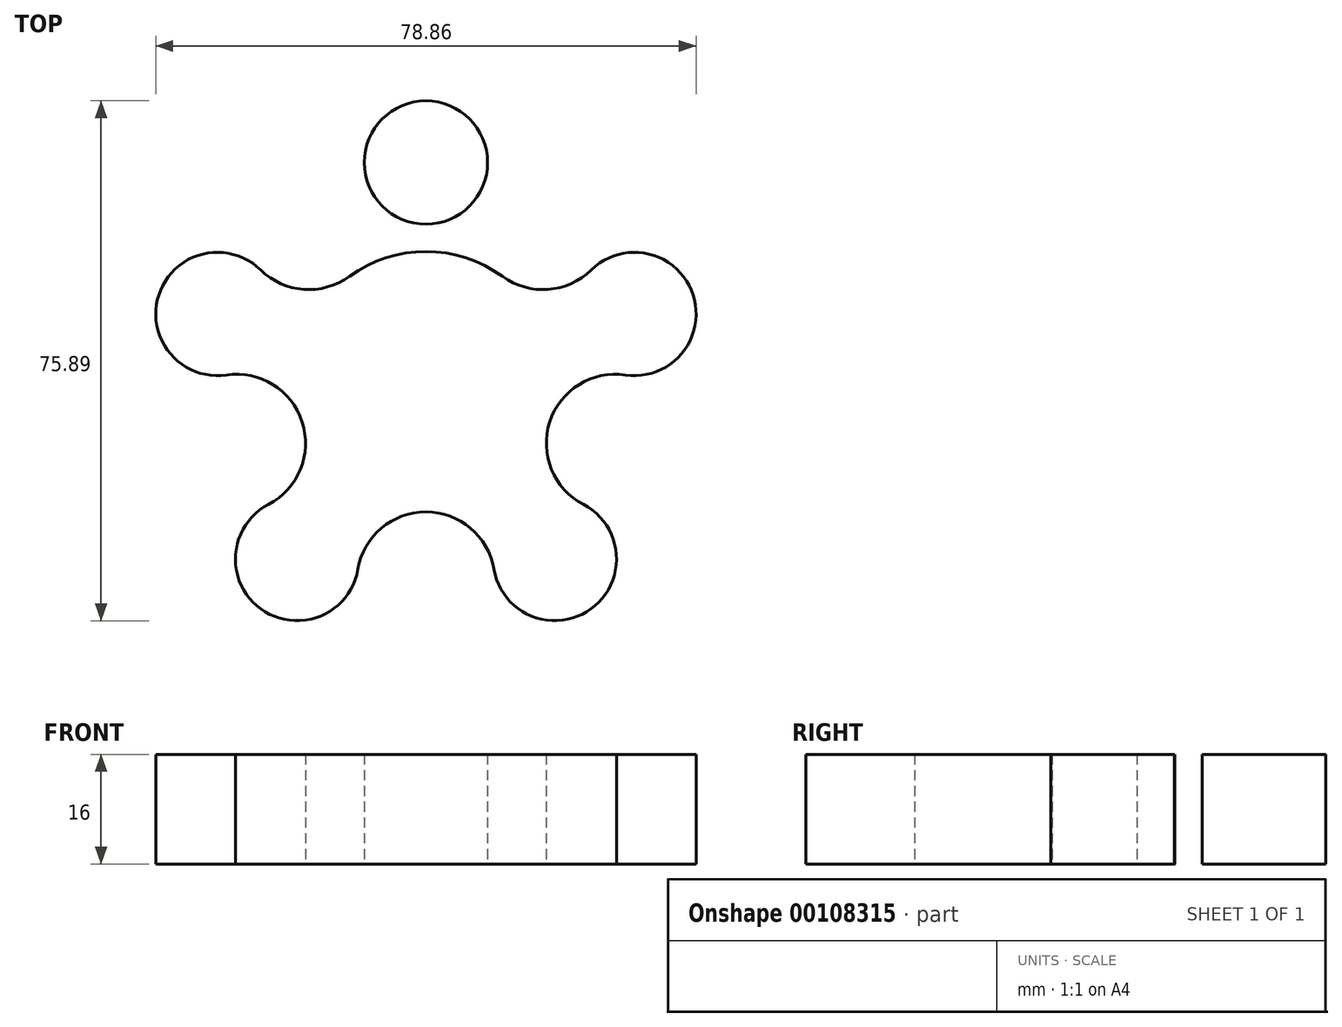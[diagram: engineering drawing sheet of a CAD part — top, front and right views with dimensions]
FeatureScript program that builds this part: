
annotation { "Feature Type Name" : "Feature", "Feature Type Description" : "" }
export const myFeature = defineFeature(function(context is Context, id is Id, definition is map)
    precondition{}
    {
        {
            var Q0;
            Q0=qCreatedBy(makeId("Top.planeOp"),FACE);
            var sketch = newSketch(context, id + "F0", { "sketchPlane" : qUnion([Q0])});
            skCircle(sketch, "E0", {"center": v(0, 0) * mm, "radius": 19 * mm});
            skLineSegment(sketch, "E1", {"start": v(0, 0) * mm, "end": v(22.05, 30.35) * mm, "construction": true});
            skLineSegment(sketch, "E2", {"start": v(-22.13, 41) * mm, "end": v(0, 41) * mm, "construction": true});
            skLineSegment(sketch, "E3", {"start": v(11.17, 15.37) * mm, "end": v(26.44, 4.28) * mm, "construction": true});
            skCircle(sketch, "E4", {"center": v(0, 32) * mm, "radius": 9 * mm});
            skArc(sketch, "E5", {"start": v(11.17, 15.37) * mm, "mid": v(7.3, 21.12) * mm, "end": v(8.06, 28) * mm});
            skArc(sketch, "E6.MirrorCS", {"start": v(-11.17, 15.37) * mm, "mid": v(-7.3, 21.12) * mm, "end": v(-8.06, 28) * mm});
            skCircle(sketch, "E7.1.0", {"center": v(-30.43, 9.89) * mm, "radius": 9 * mm});
            skArc(sketch, "E7.1.1", {"start": v(-18.07, -5.87) * mm, "mid": v(-22.34, -0.42) * mm, "end": v(-29.12, 0.98) * mm});
            skArc(sketch, "E7.1.3", {"start": v(-11.17, 15.37) * mm, "mid": v(-17.83, 13.47) * mm, "end": v(-24.14, 16.32) * mm});
            skCircle(sketch, "E7.2.0", {"center": v(-18.8, -25.89) * mm, "radius": 9 * mm});
            skArc(sketch, "E7.2.1", {"start": v(0, -19) * mm, "mid": v(-6.5, -21.38) * mm, "end": v(-9.94, -27.4) * mm});
            skArc(sketch, "E7.2.3", {"start": v(-18.07, -5.87) * mm, "mid": v(-18.32, -12.8) * mm, "end": v(-22.98, -17.91) * mm});
            skCircle(sketch, "E7.3.0", {"center": v(18.8, -25.89) * mm, "radius": 9 * mm});
            skArc(sketch, "E7.3.1", {"start": v(18.07, -5.87) * mm, "mid": v(18.32, -12.8) * mm, "end": v(22.98, -17.91) * mm});
            skArc(sketch, "E7.3.3", {"start": v(0, -19) * mm, "mid": v(6.5, -21.38) * mm, "end": v(9.94, -27.4) * mm});
            skCircle(sketch, "E7.4.0", {"center": v(30.43, 9.89) * mm, "radius": 9 * mm});
            skArc(sketch, "E7.4.1", {"start": v(11.17, 15.37) * mm, "mid": v(17.83, 13.47) * mm, "end": v(24.14, 16.32) * mm});
            skArc(sketch, "E7.4.3", {"start": v(18.07, -5.87) * mm, "mid": v(22.34, -0.42) * mm, "end": v(29.12, 0.98) * mm});
            skSolve(sketch);
        }
        {
            var Q0;
            {var subQ0=sQuery(id+"F0.wireOp",EDGE,"E4");var subQ1=makeQuery(id+"F0.imprint","INTERSECT",VERTEX,{"derivedFrom":[subQ0,sQuery(id+"F0.wireOp",EDGE,"E5")]});Q0=makeQuery(id+"F0.imprint","IMPRINT",FACE,{"disambiguationData":[TD([[makeQuery(id+"F0.imprint","IMPRINT",EDGE,{"disambiguationData":[TD([[subQ1,1.0]])],"derivedFrom":subQ0}),1.0]])]});}
            var Q1;
            {var subQ0=sQuery(id+"F0.wireOp",EDGE,"E7.4.0");var subQ1=makeQuery(id+"F0.imprint","INTERSECT",VERTEX,{"derivedFrom":[subQ0,sQuery(id+"F0.wireOp",EDGE,"E7.4.1")]});Q1=makeQuery(id+"F0.imprint","IMPRINT",FACE,{"disambiguationData":[TD([[makeQuery(id+"F0.imprint","IMPRINT",EDGE,{"disambiguationData":[TD([[subQ1,-1.0]])],"derivedFrom":subQ0}),1.0]])]});}
            var Q2;
            {var subQ0=sQuery(id+"F0.wireOp",EDGE,"E7.3.0");var subQ1=makeQuery(id+"F0.imprint","INTERSECT",VERTEX,{"derivedFrom":[subQ0,sQuery(id+"F0.wireOp",EDGE,"E7.3.1")]});Q2=makeQuery(id+"F0.imprint","IMPRINT",FACE,{"disambiguationData":[TD([[makeQuery(id+"F0.imprint","IMPRINT",EDGE,{"disambiguationData":[TD([[subQ1,-1.0]])],"derivedFrom":subQ0}),1.0]])]});}
            var Q3;
            {var subQ0=sQuery(id+"F0.wireOp",EDGE,"E7.2.0");var subQ1=makeQuery(id+"F0.imprint","INTERSECT",VERTEX,{"derivedFrom":[subQ0,sQuery(id+"F0.wireOp",EDGE,"E7.2.1")]});Q3=makeQuery(id+"F0.imprint","IMPRINT",FACE,{"disambiguationData":[TD([[makeQuery(id+"F0.imprint","IMPRINT",EDGE,{"disambiguationData":[TD([[subQ1,-1.0]])],"derivedFrom":subQ0}),1.0]])]});}
            var Q4;
            {var subQ0=sQuery(id+"F0.wireOp",EDGE,"E7.1.0");var subQ1=makeQuery(id+"F0.imprint","INTERSECT",VERTEX,{"derivedFrom":[subQ0,sQuery(id+"F0.wireOp",EDGE,"E7.1.1")]});Q4=makeQuery(id+"F0.imprint","IMPRINT",FACE,{"disambiguationData":[TD([[makeQuery(id+"F0.imprint","IMPRINT",EDGE,{"disambiguationData":[TD([[subQ1,-1.0]])],"derivedFrom":subQ0}),1.0]])]});}
            var Q5;
            {var subQ0=sQuery(id+"F0.wireOp",EDGE,"E0");var subQ5=makeQuery(id+"F0.imprint","INTERSECT",VERTEX,{"derivedFrom":[subQ0,sQuery(id+"F0.wireOp",EDGE,"E5"),sQuery(id+"F0.wireOp",EDGE,"E7.4.1")]});Q5=makeQuery(id+"F0.imprint","IMPRINT",FACE,{"disambiguationData":[TD([[makeQuery(id+"F0.imprint","IMPRINT",EDGE,{"disambiguationData":[TD([[subQ5,-1.0]])],"derivedFrom":subQ0}),1.0]])]});}
            var Q6;
            {var subQ2=sQuery(id+"F0.wireOp",EDGE,"E7.3.1");Q6=makeQuery(id+"F0.imprint","IMPRINT",FACE,{"disambiguationData":[TD([[makeQuery(id+"F0.imprint","IMPRINT",EDGE,{"derivedFrom":subQ2}),-1.0]])]});}
            var Q7;
            {var subQ2=sQuery(id+"F0.wireOp",EDGE,"E7.2.1");Q7=makeQuery(id+"F0.imprint","IMPRINT",FACE,{"disambiguationData":[TD([[makeQuery(id+"F0.imprint","IMPRINT",EDGE,{"derivedFrom":subQ2}),-1.0]])]});}
            var Q8;
            {var subQ2=sQuery(id+"F0.wireOp",EDGE,"E7.1.1");Q8=makeQuery(id+"F0.imprint","IMPRINT",FACE,{"disambiguationData":[TD([[makeQuery(id+"F0.imprint","IMPRINT",EDGE,{"derivedFrom":subQ2}),-1.0]])]});}
            var Q9;
            {var subQ0=sQuery(id+"F0.wireOp",EDGE,"E5");Q9=makeQuery(id+"F0.imprint","IMPRINT",FACE,{"disambiguationData":[TD([[makeQuery(id+"F0.imprint","IMPRINT",EDGE,{"derivedFrom":subQ0}),1.0]])]});}
            var Q10;
            {var subQ0=sQuery(id+"F0.wireOp",EDGE,"E7.4.1");Q10=makeQuery(id+"F0.imprint","IMPRINT",FACE,{"disambiguationData":[TD([[makeQuery(id+"F0.imprint","IMPRINT",EDGE,{"derivedFrom":subQ0}),-1.0]])]});}
            extrude(context, id + "F1", {"entities" : qUnion([Q0, Q1, Q2, Q3, Q4, Q5, Q6, Q7, Q8, Q9, Q10]), "depth" : 16 * mm});
        }
    });
